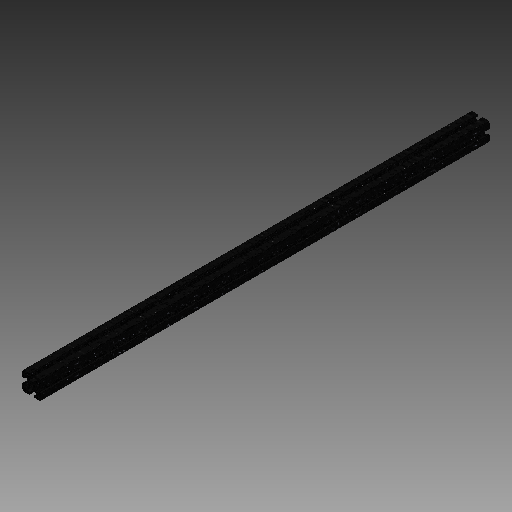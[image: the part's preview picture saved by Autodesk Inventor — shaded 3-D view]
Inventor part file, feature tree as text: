
AUTODESK INVENTOR PART (.ipt)
format: ipt  version: 2019 (Build 230136000, 136)  size: 248,832 bytes
history: native  units: in
note: dims shown in document units (in); Inventor stores cm internally (conversion verified against a paired STEP export)
features: plane x1, extrude x1, sketch x1
ambient origin geometry x8: Origin, YZ Plane, XZ Plane, XY Plane, X Axis, Y Axis, Z Axis, Center Point
bodies: Solid1 (feature_tree)
feature tree (3):
  plane  "Work Plane1"
  extrude  "Extrusion1"  [1 undecoded]
  sketch  "Sketch1"  dims[d0=36.0in d1=0.0in]
note: 1 required parameter value undecoded (feature->parameter linkage not recoverable at this tier; creation-order binding heuristic only, values carry confidence <= 0.55)
